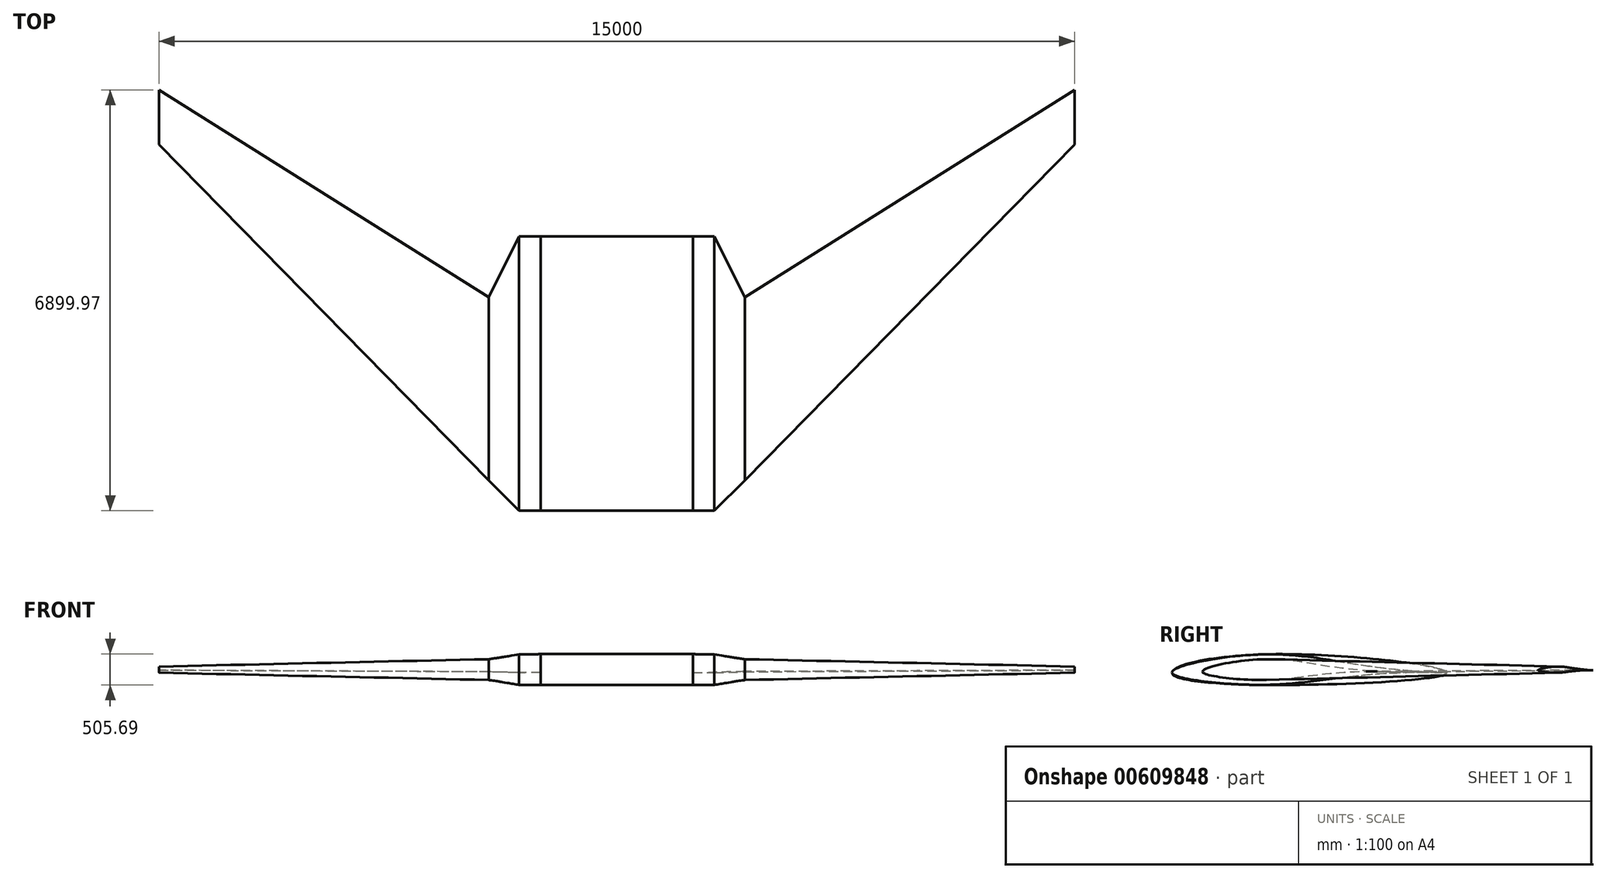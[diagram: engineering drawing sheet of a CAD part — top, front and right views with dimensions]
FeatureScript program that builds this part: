
annotation { "Feature Type Name" : "Feature", "Feature Type Description" : "" }
export const myFeature = defineFeature(function(context is Context, id is Id, definition is map)
    precondition{}
    {
        {
            var Q0;
            Q0=qCreatedBy(makeId("Right.planeOp"),FACE);
            var sketch = newSketch(context, id + "F0", { "sketchPlane" : qUnion([Q0])});
            skFitSpline(sketch, "E0", {"points": [v(-1500, -50) * mm, v(0, 250) * mm, v(3000, -50) * mm], "startDerivative": vector(0, 887.04) * mm, "endDerivative": vector(0, -631.84) * mm});
            skFitSpline(sketch, "E1", {"points": [v(-1500, -50) * mm, v(0, -250) * mm, v(3000, -50) * mm], "startDerivative": vector(0, -903.58) * mm, "endDerivative": vector(0, 641.04) * mm});
            skSolve(sketch);
        }
        {
            var Q0;
            Q0=qCreatedBy(makeId("Right.planeOp"),FACE);
            cPlane(context, id + "F1", {"entities" : qUnion([Q0]), "cplaneType" : CPlaneType.OFFSET, "offset" : 1600 * mm, "oppositeDirection" : true, "width" : 150 * mm, "height" : 150 * mm});
        }
        {
            var Q0;
            Q0=qCreatedBy(id+"F1.planeOp",FACE);
            var sketch = newSketch(context, id + "F2", { "sketchPlane" : qUnion([Q0])});
            skFitSpline(sketch, "E2", {"points": [v(-1500, -50) * mm, v(0, 250) * mm, v(3000, -50) * mm], "startDerivative": vector(0, 887.04) * mm, "endDerivative": vector(7705.35, -256.85) * mm});
            skFitSpline(sketch, "E3", {"points": [v(-1500, -50) * mm, v(0, -250) * mm, v(3000, -50) * mm], "startDerivative": vector(0, -722.87) * mm, "endDerivative": vector(7692.49, -256.42) * mm});
            skSolve(sketch);
        }
        {
            var Q0;
            Q0=qCreatedBy(makeId("Right.planeOp"),FACE);
            cPlane(context, id + "F3", {"entities" : qUnion([Q0]), "cplaneType" : CPlaneType.OFFSET, "offset" : 1600 * mm, "width" : 150 * mm, "height" : 150 * mm});
        }
        {
            var Q0;
            Q0=qCreatedBy(id+"F3.planeOp",FACE);
            var sketch = newSketch(context, id + "F4", { "sketchPlane" : qUnion([Q0])});
            skFitSpline(sketch, "E4", {"points": [v(-1500, -50) * mm, v(0, 250) * mm, v(3000, -50) * mm], "startDerivative": vector(0, 887.04) * mm, "endDerivative": vector(7705.35, -256.85) * mm});
            skFitSpline(sketch, "E5", {"points": [v(-1500, -50) * mm, v(0, -250) * mm, v(3000, -50) * mm], "startDerivative": vector(0, -722.87) * mm, "endDerivative": vector(7692.49, -256.42) * mm});
            skSolve(sketch);
        }
        {
            var Q0;
            Q0=qCreatedBy(makeId("Right.planeOp"),FACE);
            cPlane(context, id + "F5", {"entities" : qUnion([Q0]), "cplaneType" : CPlaneType.OFFSET, "offset" : 2100 * mm, "oppositeDirection" : true, "width" : 150 * mm, "height" : 150 * mm});
        }
        {
            var Q0;
            Q0=qCreatedBy(id+"F5.planeOp",FACE);
            var sketch = newSketch(context, id + "F6", { "sketchPlane" : qUnion([Q0])});
            skFitSpline(sketch, "E6", {"points": [v(-1000, -36) * mm, v(0, 170) * mm, v(2000, -36) * mm], "startDerivative": vector(0, 591.21) * mm, "endDerivative": vector(5137.83, -184.96) * mm});
            skFitSpline(sketch, "E7", {"points": [v(-1000, -36) * mm, v(0, -170) * mm, v(2000, -36) * mm], "startDerivative": vector(0, -484.31) * mm, "endDerivative": vector(5128.4, -184.62) * mm});
            skSolve(sketch);
        }
        {
            var Q0;
            Q0=qCreatedBy(makeId("Right.planeOp"),FACE);
            cPlane(context, id + "F7", {"entities" : qUnion([Q0]), "cplaneType" : CPlaneType.OFFSET, "offset" : 2100 * mm, "width" : 150 * mm, "height" : 150 * mm});
        }
        {
            var Q0;
            Q0=qCreatedBy(id+"F7.planeOp",FACE);
            var sketch = newSketch(context, id + "F8", { "sketchPlane" : qUnion([Q0])});
            skFitSpline(sketch, "E8", {"points": [v(-1000, -36) * mm, v(0, 170) * mm, v(2000, -36) * mm], "startDerivative": vector(0, 591.21) * mm, "endDerivative": vector(5137.83, -184.96) * mm});
            skFitSpline(sketch, "E9", {"points": [v(-1000, -36) * mm, v(0, -170) * mm, v(2000, -36) * mm], "startDerivative": vector(0, -484.31) * mm, "endDerivative": vector(5128.4, -184.62) * mm});
            skSolve(sketch);
        }
        {
            var Q0;
            Q0=qCreatedBy(makeId("Right.planeOp"),FACE);
            cPlane(context, id + "F9", {"entities" : qUnion([Q0]), "cplaneType" : CPlaneType.OFFSET, "offset" : 7500 * mm, "oppositeDirection" : true, "width" : 150 * mm, "height" : 150 * mm});
        }
        {
            var Q0;
            Q0=qCreatedBy(id+"F9.planeOp",FACE);
            var sketch = newSketch(context, id + "F10", { "sketchPlane" : qUnion([Q0])});
            skFitSpline(sketch, "E10", {"points": [v(4500, -10) * mm, v(4800, 50) * mm, v(5400, -10) * mm], "startDerivative": vector(0, 177.4) * mm, "endDerivative": vector(1541.07, -51.37) * mm});
            skFitSpline(sketch, "E11", {"points": [v(4500, -10) * mm, v(4800, -50) * mm, v(5400, -10) * mm], "startDerivative": vector(0, -144.57) * mm, "endDerivative": vector(1538.5, -51.28) * mm});
            skSolve(sketch);
        }
        {
            var Q0;
            Q0=qCreatedBy(makeId("Right.planeOp"),FACE);
            cPlane(context, id + "F11", {"entities" : qUnion([Q0]), "cplaneType" : CPlaneType.OFFSET, "offset" : 7500 * mm, "width" : 150 * mm, "height" : 150 * mm});
        }
        {
            var Q0;
            Q0=qCreatedBy(id+"F11.planeOp",FACE);
            var sketch = newSketch(context, id + "F12", { "sketchPlane" : qUnion([Q0])});
            skFitSpline(sketch, "E12", {"points": [v(4500, -10) * mm, v(4800, 50) * mm, v(5400, -10) * mm], "startDerivative": vector(0, 177.4) * mm, "endDerivative": vector(1541.07, -51.37) * mm});
            skFitSpline(sketch, "E13", {"points": [v(4500, -10) * mm, v(4800, -50) * mm, v(5400, -10) * mm], "startDerivative": vector(0, -144.57) * mm, "endDerivative": vector(1538.5, -51.28) * mm});
            skSolve(sketch);
        }
        {
            var Q0;
            Q0=makeQuery(id+"F0.imprint","IMPRINT",FACE,{"disambiguationData":[TD([[makeQuery(id+"F0.imprint","IMPRINT",EDGE,{"derivedFrom":sQuery(id+"F0.wireOp",EDGE,"E0")}),-1.0]])]});
            extrude(context, id + "F13", {"entities" : qUnion([Q0]), "endBound" : BoundingType.SYMMETRIC, "depth" : 2500 * mm, "offsetDistance" : 25 * mm});
        }
        {
            var Q1;
            Q1=makeQuery(id+"F13.opExtrude","CAP_FACE",FACE,{"disambiguationData":[OSD([sQuery(id+"F0.wireOp",EDGE,"E0"),sQuery(id+"F0.wireOp",EDGE,"E1")])],"isStart":true});
            var Q2;
            {var subQ0=sQuery(id+"F2.wireOp",EDGE,"E2");Q2=makeQuery(id+"F2.imprint","IMPRINT",FACE,{"disambiguationData":[TD([[makeQuery(id+"F2.imprint","IMPRINT",EDGE,{"derivedFrom":subQ0}),-1.0]])]});}
            loft(context, id + "F14", {"operationType" : NewBodyOperationType.ADD, "sheetProfilesArray" : [{ "sheetProfileEntities" : qUnion([Q1]) }, { "sheetProfileEntities" : qUnion([Q2]) }]});
        }
        {
            var Q1;
            Q1=makeQuery(id+"F13.opExtrude","CAP_FACE",FACE,{"disambiguationData":[OSD([sQuery(id+"F0.wireOp",EDGE,"E0"),sQuery(id+"F0.wireOp",EDGE,"E1")])],"isStart":false});
            var Q2;
            {var subQ0=sQuery(id+"F4.wireOp",EDGE,"E4");Q2=makeQuery(id+"F4.imprint","IMPRINT",FACE,{"disambiguationData":[TD([[makeQuery(id+"F4.imprint","IMPRINT",EDGE,{"derivedFrom":subQ0}),-1.0]])]});}
            loft(context, id + "F15", {"operationType" : NewBodyOperationType.ADD, "sheetProfilesArray" : [{ "sheetProfileEntities" : qUnion([Q1]) }, { "sheetProfileEntities" : qUnion([Q2]) }]});
        }
        {
            var Q1;
            {var subQ0=sQuery(id+"F2.wireOp",EDGE,"E2");Q1=makeQuery(id+"F14.opLoft","CAP_FACE",FACE,{"disambiguationData":[OSD([makeQuery(id+"F2.imprint","IMPRINT",FACE,{"disambiguationData":[TD([[makeQuery(id+"F2.imprint","IMPRINT",EDGE,{"derivedFrom":subQ0}),-1.0]])]})])],"isStart":true});}
            var Q2;
            {var subQ0=sQuery(id+"F6.wireOp",EDGE,"E6");Q2=makeQuery(id+"F6.imprint","IMPRINT",FACE,{"disambiguationData":[TD([[makeQuery(id+"F6.imprint","IMPRINT",EDGE,{"derivedFrom":subQ0}),-1.0]])]});}
            loft(context, id + "F16", {"operationType" : NewBodyOperationType.ADD, "sheetProfilesArray" : [{ "sheetProfileEntities" : qUnion([Q1]) }, { "sheetProfileEntities" : qUnion([Q2]) }]});
        }
        {
            var Q1;
            {var subQ0=sQuery(id+"F4.wireOp",EDGE,"E4");Q1=makeQuery(id+"F15.opLoft","CAP_FACE",FACE,{"disambiguationData":[OSD([makeQuery(id+"F4.imprint","IMPRINT",FACE,{"disambiguationData":[TD([[makeQuery(id+"F4.imprint","IMPRINT",EDGE,{"derivedFrom":subQ0}),-1.0]])]})])],"isStart":true});}
            var Q2;
            {var subQ0=sQuery(id+"F8.wireOp",EDGE,"E8");Q2=makeQuery(id+"F8.imprint","IMPRINT",FACE,{"disambiguationData":[TD([[makeQuery(id+"F8.imprint","IMPRINT",EDGE,{"derivedFrom":subQ0}),-1.0]])]});}
            loft(context, id + "F17", {"operationType" : NewBodyOperationType.ADD, "sheetProfilesArray" : [{ "sheetProfileEntities" : qUnion([Q1]) }, { "sheetProfileEntities" : qUnion([Q2]) }]});
        }
        {
            var Q1;
            {var subQ0=sQuery(id+"F6.wireOp",EDGE,"E6");Q1=makeQuery(id+"F16.opLoft","CAP_FACE",FACE,{"disambiguationData":[OSD([makeQuery(id+"F6.imprint","IMPRINT",FACE,{"disambiguationData":[TD([[makeQuery(id+"F6.imprint","IMPRINT",EDGE,{"derivedFrom":subQ0}),-1.0]])]})])],"isStart":true});}
            var Q2;
            {var subQ0=sQuery(id+"F10.wireOp",EDGE,"E10");Q2=makeQuery(id+"F10.imprint","IMPRINT",FACE,{"disambiguationData":[TD([[makeQuery(id+"F10.imprint","IMPRINT",EDGE,{"derivedFrom":subQ0}),-1.0]])]});}
            loft(context, id + "F18", {"operationType" : NewBodyOperationType.ADD, "sheetProfilesArray" : [{ "sheetProfileEntities" : qUnion([Q1]) }, { "sheetProfileEntities" : qUnion([Q2]) }]});
        }
        {
            var Q1;
            {var subQ0=sQuery(id+"F8.wireOp",EDGE,"E8");Q1=makeQuery(id+"F17.opLoft","CAP_FACE",FACE,{"disambiguationData":[OSD([makeQuery(id+"F8.imprint","IMPRINT",FACE,{"disambiguationData":[TD([[makeQuery(id+"F8.imprint","IMPRINT",EDGE,{"derivedFrom":subQ0}),-1.0]])]})])],"isStart":true});}
            var Q2;
            {var subQ0=sQuery(id+"F12.wireOp",EDGE,"E12");Q2=makeQuery(id+"F12.imprint","IMPRINT",FACE,{"disambiguationData":[TD([[makeQuery(id+"F12.imprint","IMPRINT",EDGE,{"derivedFrom":subQ0}),-1.0]])]});}
            loft(context, id + "F19", {"operationType" : NewBodyOperationType.ADD, "sheetProfilesArray" : [{ "sheetProfileEntities" : qUnion([Q1]) }, { "sheetProfileEntities" : qUnion([Q2]) }]});
        }
    });
